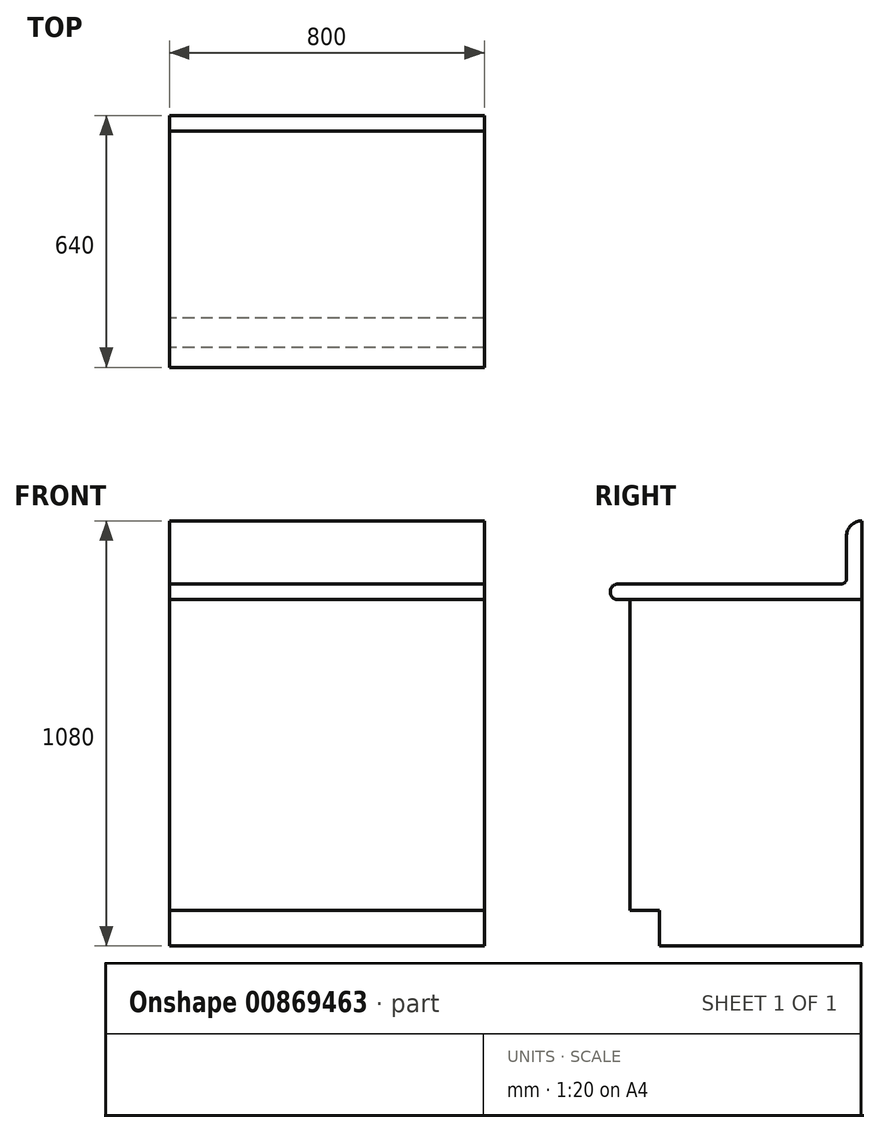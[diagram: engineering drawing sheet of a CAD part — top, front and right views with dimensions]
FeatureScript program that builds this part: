
annotation { "Feature Type Name" : "Feature", "Feature Type Description" : "" }
export const myFeature = defineFeature(function(context is Context, id is Id, definition is map)
    precondition{}
    {
        {
            var Q0;
            Q0=qCreatedBy(makeId("Top.planeOp"),FACE);
            var sketch = newSketch(context, id + "F0", { "sketchPlane" : qUnion([Q0])});
            skLineSegment(sketch, "E0.bottom", {"start": v(0, 0) * mm, "end": v(800, 0) * mm});
            skLineSegment(sketch, "E0.top", {"start": v(0, 590) * mm, "end": v(800, 590) * mm});
            skLineSegment(sketch, "E0.left", {"start": v(0, 0) * mm, "end": v(0, 590) * mm});
            skLineSegment(sketch, "E0.right", {"start": v(800, 0) * mm, "end": v(800, 590) * mm});
            skSolve(sketch);
        }
        {
            var Q0;
            Q0=qSketchRegion(id+"F0",true);
            extrude(context, id + "F1", {"entities" : qUnion([Q0]), "depth" : 880 * mm, "offsetDistance" : 25 * mm});
        }
        {
            var Q0;
            Q0=qCreatedBy(makeId("Right.planeOp"),FACE);
            var sketch = newSketch(context, id + "F2", { "sketchPlane" : qUnion([Q0])});
            skLineSegment(sketch, "E1.bottom", {"start": v(0, 0) * mm, "end": v(75, 0) * mm});
            skLineSegment(sketch, "E1.top", {"start": v(0, 90) * mm, "end": v(75, 90) * mm});
            skLineSegment(sketch, "E1.left", {"start": v(0, 0) * mm, "end": v(0, 90) * mm});
            skLineSegment(sketch, "E1.right", {"start": v(75, 0) * mm, "end": v(75, 90) * mm});
            skSolve(sketch);
        }
        {
            var Q0;
            Q0=qSketchRegion(id+"F2",true);
            extrude(context, id + "F3", {"entities" : qUnion([Q0]), "operationType" : NewBodyOperationType.REMOVE, "endBound" : BoundingType.THROUGH_ALL, "depth" : 25 * mm, "offsetDistance" : 25 * mm});
        }
        {
            var Q0;
            Q0=qCreatedBy(makeId("Right.planeOp"),FACE);
            var sketch = newSketch(context, id + "F4", { "sketchPlane" : qUnion([Q0])});
            skLineSegment(sketch, "E2.0", {"start": v(0, 880) * mm, "end": v(590, 880) * mm, "construction": true});
            skLineSegment(sketch, "E3.bottom", {"start": v(590, 880) * mm, "end": v(-30, 880) * mm});
            skLineSegment(sketch, "E3.top", {"start": v(537.3, 920) * mm, "end": v(-30, 920) * mm});
            skLineSegment(sketch, "E3.left", {"start": v(590, 880) * mm, "end": v(590, 1080) * mm});
            skLineSegment(sketch, "E3.right", {"start": v(-50, 880) * mm, "end": v(-50, 920) * mm, "construction": true});
            skArc(sketch, "E4", {"start": v(-30, 920) * mm, "mid": v(-50, 900) * mm, "end": v(-30, 880) * mm});
            skLineSegment(sketch, "E5", {"start": v(550, 932.7) * mm, "end": v(550, 1040) * mm});
            skLineSegment(sketch, "E6", {"start": v(590, 1080) * mm, "end": v(590, 1080) * mm});
            skPoint(sketch, "E7.visualSharp", {"position": v(550, 1080) * mm});
            skArc(sketch, "E7.filletArc", {"start": v(590, 1080) * mm, "mid": v(561.72, 1068.28) * mm, "end": v(550, 1040) * mm});
            skPoint(sketch, "E8.newPointA", {"position": v(590, 920) * mm});
            skArc(sketch, "E8.filletArc", {"start": v(537.3, 920) * mm, "mid": v(546.28, 923.72) * mm, "end": v(550, 932.7) * mm});
            skSolve(sketch);
        }
        {
            var Q0;
            Q0=qSketchRegion(id+"F4",true);
            var Q1;
            Q1=makeQuery(id+"F1.opExtrude","SWEPT_FACE",FACE,{"disambiguationData":[OSD([sQuery(id+"F0.wireOp",EDGE,"E0.right")])]});
            extrude(context, id + "F5", {"entities" : qUnion([Q0]), "endBound" : BoundingType.UP_TO_SURFACE, "depth" : 25 * mm, "endBoundEntityFace" : qUnion([Q1]), "offsetDistance" : 25 * mm});
        }
    });
